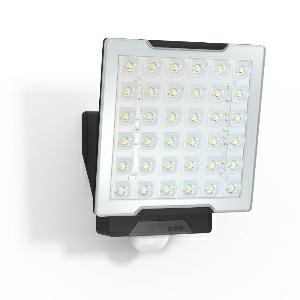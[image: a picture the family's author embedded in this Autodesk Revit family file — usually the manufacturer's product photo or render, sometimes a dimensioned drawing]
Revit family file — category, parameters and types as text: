
# Revit family: xled_pro_square_xl_009946
name_source: partatom
category: Leuchten
revit_build: Autodesk Revit 2016 (Build: 20190508_0715(x64)
units: mm (PartAtom-declared; Revit-internal decimal feet)

## family parameters
Basisbauteil = Fläche
Beim Laden mit Abzugskörper schneiden = Nein
Bemaßung runder Anschluss = Durchmesser verwenden
Gemeinsam genutzt = Nein
Lichtquelle = Nein
Raumberechnungspunkt = Nein
Teiletyp = Normal

## types (1)
- XLED PRO Square XL (1 x , 4400 lm, 4000 K)
    Beschreibung = Dimensions (L x W x H): 130 x 178 x 230 mm; Mains power supply: 220 – 240 V / 50 – 60 Hz; Mounting height max.: 6,00 m; Sensor Technology: passive infrared; Output: 48 W; Interconnection: Yes; Type of interconnection: Sensor/slave; Interconnection, number: maximum of 10 floodlights; Luminous flux: 4400 lm; Colour temperature: 4000 K; Colour variation LED: SDCM3; Colour Rendering Index CRI: 80-89; With lamp: Yes, STEINEL LED system; Lamp: LED cannot be replaced; LED life expectancy (max. °C): 50000 h; Drop in luminous flux in accordance with LM80: L70B10; LED cooling system: Passive Thermo Control; With motion detector: Yes; Detection angle: 240 °; Angle of aperture: 180 °; Sneak-by guard: Yes; Capability of masking out individual segments: Yes; Reach, radial: r = 5 m (52 m²); Reach, tangential: r = 12 m (302 m²); Photo-cell controller: Yes; Twilight setting: 2 – 1000 lx; Time setting: 5 sec – 15 min; Basic light level function: Yes; Basic light level function time: 10 min, 30 min, all night; Soft light start: No; Continuous light: selectable, 4h; Impact resistance: IK03; IP-rating: IP54; Protection class: I; Ambient temperature: -20 – 40 °C; Housing material: Aluminium; Cover material: Plastic, transparent; Manufacturer's Warranty: 5 years; PU1, net weight: 1,818 kg; Version: black; PU1, EAN: 4007841009946
    CIE Flux Codes = 53 87 98 99 100
    Color Rendering = 80-89
    Color Temperature = 4000 K
    Frequency = 60 Hz, 50 Hz
    Height = 230 mm
    Hersteller = Steinel
    Lamp Light Flux = 4400 lm
    Lamp count = 1
    Lampe = 1 x
    Length = 130 mm
    Luminous efficacy = 92 lm/W
    ModVariant = Nein
    Modell = 009946
    Mounting Type = Surface mounted
    Number of Poles = 1
    OnlyDefault = Ja
    Power Factor = 1
    Product Name = XLED PRO Square XL
    Product group = Sensor-switched indoor light
    ProductGroupID = 30
    Protection Class = Protection class I
    Protection Degree = IP 54
    RlxData = <blob elided: 133589 chars, md5=27c3d62f>
    Scheinlast = 48 VA
    Socket = socket
    Standby Power = 0 W
    System Light Flux = 4400 lm
    System Power = 48 W
    Typenbild = produkt1_009946.jpg
    Typenkommentare = Product without accessories
    URL = http://relux.com
    VarID = ---
    Voltage = 0 V
    Vorgabe-Ansicht = 1800 mm
    Weight = 0.00 kg
    Width = 178 mm

## geometry (parser evidence)
native form markers: Sweep x10
no freeform markers — native parametric forms only
